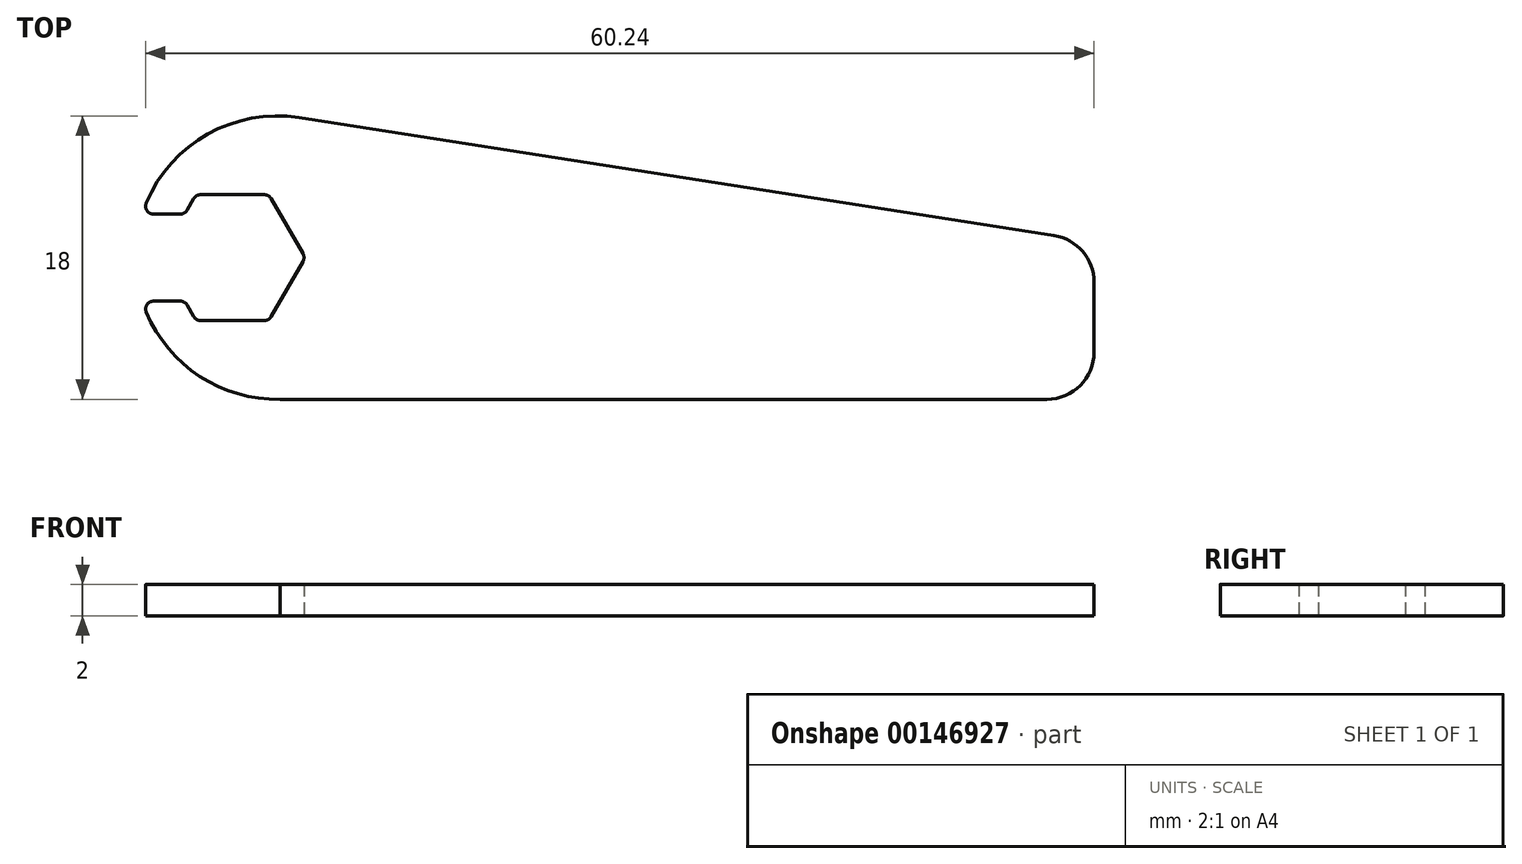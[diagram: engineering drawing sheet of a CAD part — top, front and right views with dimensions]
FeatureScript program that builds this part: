
annotation { "Feature Type Name" : "Feature", "Feature Type Description" : "" }
export const myFeature = defineFeature(function(context is Context, id is Id, definition is map)
    precondition{}
    {
        {
            var Q0;
            Q0=qCreatedBy(makeId("Top.planeOp"),FACE);
            var sketch = newSketch(context, id + "F0", { "sketchPlane" : qUnion([Q0])});
            skCircle(sketch, "E0.cCircle", {"center": v(-81.88, 8) * mm, "radius": 4 * mm, "construction": true});
            skLineSegment(sketch, "E0.0", {"start": v(-79.85, 4) * mm, "end": v(-83.9, 4) * mm});
            skLineSegment(sketch, "E0.1", {"start": v(-84.33, 4.25) * mm, "end": v(-84.75, 4.99) * mm});
            skLineSegment(sketch, "E0.2", {"start": v(-84.75, 11.02) * mm, "end": v(-84.33, 11.75) * mm});
            skLineSegment(sketch, "E0.3", {"start": v(-83.9, 12) * mm, "end": v(-79.85, 12) * mm});
            skLineSegment(sketch, "E0.4", {"start": v(-79.42, 11.75) * mm, "end": v(-77.4, 8.25) * mm});
            skLineSegment(sketch, "E0.5", {"start": v(-77.4, 7.75) * mm, "end": v(-79.42, 4.25) * mm});
            skPoint(sketch, "E0.0.midPoint", {"position": v(-81.88, 4) * mm});
            skArc(sketch, "E1", {"start": v(-87.35, 4.55) * mm, "mid": v(-83.96, 0.47) * mm, "end": v(-78.86, -1) * mm});
            skLineSegment(sketch, "E2", {"start": v(-85.19, 10.77) * mm, "end": v(-86.9, 10.77) * mm});
            skLineSegment(sketch, "E3", {"start": v(-86.5, 8) * mm, "end": v(-88.04, 8) * mm, "construction": true});
            skLineSegment(sketch, "E4.MirrorCS", {"start": v(-85.19, 5.24) * mm, "end": v(-86.9, 5.24) * mm});
            skPoint(sketch, "E5.visualSharp", {"position": v(-87.6, 10.77) * mm});
            skArc(sketch, "E5.filletArc", {"start": v(-87.35, 11.46) * mm, "mid": v(-87.3, 11) * mm, "end": v(-86.9, 10.77) * mm});
            skPoint(sketch, "E6.visualSharp", {"position": v(-84.9, 10.77) * mm});
            skArc(sketch, "E6.filletArc", {"start": v(-85.19, 10.77) * mm, "mid": v(-84.94, 10.84) * mm, "end": v(-84.75, 11.02) * mm});
            skPoint(sketch, "E7.visualSharp", {"position": v(-84.19, 12) * mm});
            skArc(sketch, "E7.filletArc", {"start": v(-83.9, 12) * mm, "mid": v(-84.15, 11.94) * mm, "end": v(-84.33, 11.75) * mm});
            skPoint(sketch, "E8.visualSharp", {"position": v(-79.57, 12) * mm});
            skArc(sketch, "E8.filletArc", {"start": v(-79.42, 11.75) * mm, "mid": v(-79.6, 11.94) * mm, "end": v(-79.85, 12) * mm});
            skPoint(sketch, "E9.visualSharp", {"position": v(-77.26, 8) * mm});
            skArc(sketch, "E9.filletArc", {"start": v(-77.4, 7.75) * mm, "mid": v(-77.33, 8) * mm, "end": v(-77.4, 8.25) * mm});
            skPoint(sketch, "E10.visualSharp", {"position": v(-79.57, 4) * mm});
            skArc(sketch, "E10.filletArc", {"start": v(-79.85, 4) * mm, "mid": v(-79.6, 4.07) * mm, "end": v(-79.42, 4.25) * mm});
            skPoint(sketch, "E11.visualSharp", {"position": v(-84.19, 4) * mm});
            skArc(sketch, "E11.filletArc", {"start": v(-84.33, 4.25) * mm, "mid": v(-84.15, 4.07) * mm, "end": v(-83.9, 4) * mm});
            skPoint(sketch, "E12.visualSharp", {"position": v(-84.9, 5.24) * mm});
            skArc(sketch, "E12.filletArc", {"start": v(-84.75, 4.99) * mm, "mid": v(-84.94, 5.17) * mm, "end": v(-85.19, 5.24) * mm});
            skPoint(sketch, "E13.visualSharp", {"position": v(-87.6, 5.24) * mm});
            skArc(sketch, "E13.filletArc", {"start": v(-86.9, 5.24) * mm, "mid": v(-87.3, 5.02) * mm, "end": v(-87.35, 4.55) * mm});
            skLineSegment(sketch, "E14", {"start": v(-79.23, -1) * mm, "end": v(-30.15, -1) * mm});
            skLineSegment(sketch, "E15", {"start": v(-27.15, 2) * mm, "end": v(-27.15, 6.44) * mm});
            skLineSegment(sketch, "E16", {"start": v(-29.69, 9.4) * mm, "end": v(-77.65, 16.9) * mm});
            skArc(sketch, "E17.trimOffspring", {"start": v(-77.65, 16.9) * mm, "mid": v(-83.44, 15.86) * mm, "end": v(-87.35, 11.46) * mm});
            skPoint(sketch, "E18.visualSharp", {"position": v(-27.15, 9) * mm});
            skArc(sketch, "E18.filletArc", {"start": v(-27.15, 6.44) * mm, "mid": v(-27.87, 8.39) * mm, "end": v(-29.69, 9.4) * mm});
            skPoint(sketch, "E19.visualSharp", {"position": v(-27.15, -1) * mm});
            skArc(sketch, "E19.filletArc", {"start": v(-30.15, -1) * mm, "mid": v(-28.03, -0.11) * mm, "end": v(-27.15, 2) * mm});
            skSolve(sketch);
        }
        {
            var Q0;
            Q0 = qSketchRegion(id + "F0", true);
            extrude(context, id + "F1", {"entities" : qUnion([Q0]), "depth" : 2 * mm});
        }
    });
